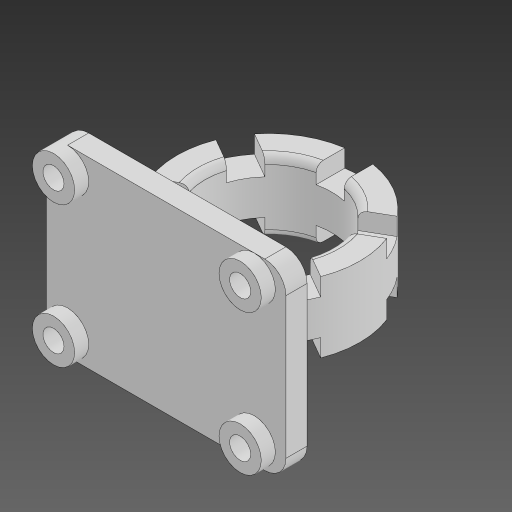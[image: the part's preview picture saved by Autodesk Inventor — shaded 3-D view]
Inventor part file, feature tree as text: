
AUTODESK INVENTOR PART (.ipt)
format: ipt  version: 2023.2 (Build 272271000, 271)  size: 359,936 bytes
history: native  units: mm
features: extrude x4, sketch x4, fillet x3, plane x2, hole x2, pattern_circular x1, mirror x1, projected_geometry x1
ambient origin geometry x8: Origin, YZ Plane, XZ Plane, XY Plane, X Axis, Y Axis, Z Axis, Center Point
bodies: Solid1 (feature_tree)
feature tree (18):
  extrude  "Extrusion1"  Depth=4.0mm
  plane  "Work Plane1"
  sketch  "Sketch2"  dims[d2=10.0mm d3=0.0mm d4=13.0mm]
  extrude  "Extrusion2"  Depth=10.0mm
  hole  "Hole1"  [1 undecoded]
  hole  "Hole2"  [1 undecoded]
  fillet  "Fillet1"  Radius=3.0mm
  extrude  "Extrusion3"  Depth=3.0mm
  pattern_circular  "Circular Pattern1"  [2 undecoded]
  plane  "Work Plane2"
  mirror  "Mirror1"
  fillet  "Fillet2"  Radius=8.0mm
  fillet  "Fillet3"  Radius=3.0mm
  extrude  "Extrusion4"  Depth=3.0mm
  sketch  "Sketch1"  dims[d0=18.0mm d1=4.0mm]
  sketch  "Sketch3"  dims[d5=34.0mm d6=26.0mm]
  sketch  "Sketch4"  dims[d7=20.0mm d8=26.5mm d9=3.0mm d10=3.0mm d11=17.0mm d12=8.0mm d13=3.0mm d14=0.0mm d15=3.0mm d16=6.0mm d17=4.0mm d18=2.0mm d19=90.0deg d20=12.0mm d21=0.0mm d22=3.0mm d23=6.0mm d24=4.0mm d25=2.0mm d26=90.0deg d27=12.0mm d28=0.0mm d29=3.0mm d30=4.0mm d31=6.0mm d32=2.0mm d33=8.0mm d34=2.5mm d35=0.0mm d36=60.0mm d37=360.0deg d39=-5.0mm d40=2.0mm d41=1.0mm d42=1.5mm d43=1.5mm d44=1.5mm d45=1.5mm d46=2.0mm d47=0.0mm d48=0.0mm d49=0.0mm d50=0.0mm d51=0.0mm]
  projected_geometry  "Projected Loop1"
note: 4 required parameter values undecoded (feature->parameter linkage not recoverable at this tier; creation-order binding heuristic only, values carry confidence <= 0.55)
